# Revit family: AFX-Dax-Sconce+
name_source: partatom
category: Lighting Fixtures
units: mm (PartAtom-declared; Revit-internal decimal feet)

## family parameters
Cut with Voids When Loaded = No
Host = Face
Light Source = Yes
Part Type = Normal
Room Calculation Point = No
Round Connector Dimension = Use Diameter
Shared = No

## types (2) — shared parameters
Apparent Load = 0 VA
Assembly Code = D5020200
Body Finish = AFX - Satin Nickel
Color Filter = 16777215
Color Rendering Index = 90
Default Elevation = 48"
Depth = 4"
Dimming Lamp Color Temperature Shift = <None>
Emit Shape Visible in Rendering = No
Emit from Rectangle Width = 4"
Lamp = LED
Manufacturer = AFX Inc
Model = DAXV27
Product Documentation Link = https://www.afxinc.com
Revit Model Built By = https://servex-us.com
Screen Finish = AFX - Diffuser
Tilt Angle = 90.00°
Type Comments = DAX
URL = https://www.afxinc.com
Voltage = 120 V
Wattage Comments = 19W
Width = 4"

## per-type parameters (varying)
| type | Description | Emit from Rectangle Length | Length | Photometric Web File |
| DAXV27 | 27'' LED Vanity | 27 1/4" | 27 1/4" | DAXV2705L30D1xx_IES.IES |
| DAXV36 | 36'' LED Vanity | 31 1/8" | 31 1/8" | DAXV3605L30D1xx_IES.IES |

## geometry (parser evidence)
native form markers: Sweep x2
no freeform markers — native parametric forms only
